AUTODESK INVENTOR PART (.ipt)
format: ipt  version: 2013 (Build 170138000, 138)  size: 86,528 bytes
history: native  units: in
note: dims shown in document units (in); Inventor stores cm internally (conversion verified against a paired STEP export)
features: sketch x1
ambient origin geometry x8: Origin, YZ Plane, XZ Plane, XY Plane, X Axis, Y Axis, Z Axis, Center Point
feature tree (1):
  sketch  "Sketch1"  dims[d0=42.0in d1=3.5in d23=19.5in d24=2.5in d25=19.5in d26=6.0in d27=13.0in d28=1.35in d29=1.205in d30=0.75in d32=30.0deg d33=33.5in d34=43.9186in d35=30.0deg d43=19.5in d44=2.5in d45=6.0in d46=13.0in d47=1.35in d48=1.205in d49=0.75in d50=0.1615in d51=33.5in d52=42.0816in]
